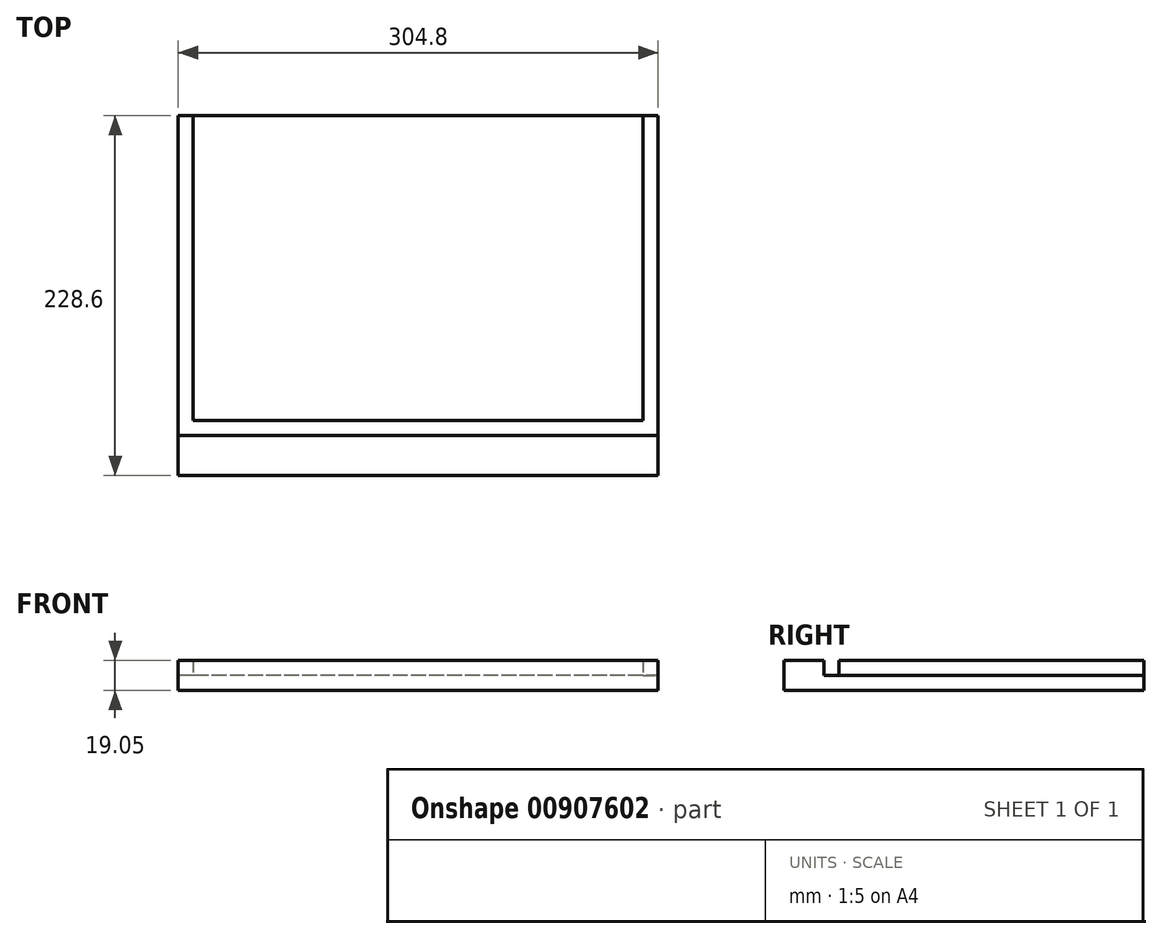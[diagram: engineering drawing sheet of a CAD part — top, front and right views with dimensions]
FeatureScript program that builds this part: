
annotation { "Feature Type Name" : "Feature", "Feature Type Description" : "" }
export const myFeature = defineFeature(function(context is Context, id is Id, definition is map)
    precondition{}
    {
        {
            var Q0;
            Q0=qCreatedBy(makeId("Top.planeOp"),FACE);
            var sketch = newSketch(context, id + "F0", { "sketchPlane" : qUnion([Q0])});
            skLineSegment(sketch, "E0.bottom", {"start": v(152.4, -114.3) * mm, "end": v(-152.4, -114.3) * mm});
            skLineSegment(sketch, "E0.top", {"start": v(152.4, 114.3) * mm, "end": v(-152.4, 114.3) * mm});
            skLineSegment(sketch, "E0.left", {"start": v(152.4, -114.3) * mm, "end": v(152.4, 114.3) * mm});
            skLineSegment(sketch, "E0.right", {"start": v(-152.4, -114.3) * mm, "end": v(-152.4, 114.3) * mm});
            skPoint(sketch, "E0.middle", {"position": v(0, 0) * mm});
            skSolve(sketch);
        }
        {
            var Q0;
            Q0 = qSketchRegion(id + "F0", true);
            extrude(context, id + "F1", {"entities" : qUnion([Q0]), "depth" : 19.05 * mm, "offsetDistance" : 25.4 * mm});
        }
        {
            var Q0;
            Q0=makeQuery(id+"F1.opExtrude","CAP_FACE",FACE,{"disambiguationData":[OSD([sQuery(id+"F0.wireOp",EDGE,"E0.bottom"),sQuery(id+"F0.wireOp",EDGE,"E0.top"),sQuery(id+"F0.wireOp",EDGE,"E0.left"),sQuery(id+"F0.wireOp",EDGE,"E0.right")])],"isStart":false});
            var sketch = newSketch(context, id + "F2", { "sketchPlane" : qUnion([Q0])});
            skLineSegment(sketch, "E1", {"start": v(0, -114.3) * mm, "end": v(0, -84.14) * mm});
            skLineSegment(sketch, "E2.bottom", {"start": v(188.14, -79.38) * mm, "end": v(-188.14, -79.38) * mm});
            skLineSegment(sketch, "E2.top", {"start": v(188.14, -88.9) * mm, "end": v(-188.14, -88.9) * mm});
            skLineSegment(sketch, "E2.left", {"start": v(188.14, -79.38) * mm, "end": v(188.14, -88.9) * mm});
            skLineSegment(sketch, "E2.right", {"start": v(-188.14, -79.38) * mm, "end": v(-188.14, -88.9) * mm});
            skPoint(sketch, "E2.middle", {"position": v(0, -84.14) * mm});
            skSolve(sketch);
        }
        {
            var Q0;
            Q0 = qSketchRegion(id + "F2", true);
            extrude(context, id + "F3", {"entities" : qUnion([Q0]), "operationType" : NewBodyOperationType.REMOVE, "oppositeDirection" : true, "depth" : 9.52 * mm, "offsetDistance" : 25.4 * mm});
        }
        {
            var Q0;
            Q0=makeQuery(id+"F1.opExtrude","SWEPT_FACE",FACE,{"disambiguationData":[OSD([sQuery(id+"F0.wireOp",EDGE,"E0.right")])]});
            var sketch = newSketch(context, id + "F4", { "sketchPlane" : qUnion([Q0])});
            skLineSegment(sketch, "E3.bottom", {"start": v(79.38, 28.57) * mm, "end": v(-114.3, 28.57) * mm});
            skLineSegment(sketch, "E3.top", {"start": v(79.38, 9.53) * mm, "end": v(-114.3, 9.53) * mm});
            skLineSegment(sketch, "E3.left", {"start": v(79.38, 28.57) * mm, "end": v(79.38, 9.53) * mm});
            skLineSegment(sketch, "E3.right", {"start": v(-114.3, 28.57) * mm, "end": v(-114.3, 9.53) * mm});
            skPoint(sketch, "E3.middle", {"position": v(-17.46, 19.05) * mm});
            skSolve(sketch);
        }
        {
            var Q0;
            Q0 = qSketchRegion(id + "F4", true);
            extrude(context, id + "F5", {"entities" : qUnion([Q0]), "operationType" : NewBodyOperationType.REMOVE, "oppositeDirection" : true, "depth" : 9.52 * mm, "offsetDistance" : 25.4 * mm});
        }
        {
            var Q0;
            Q0=makeQuery(id+"F1.opExtrude","SWEPT_FACE",FACE,{"disambiguationData":[OSD([sQuery(id+"F0.wireOp",EDGE,"E0.left")])]});
            var sketch = newSketch(context, id + "F6", { "sketchPlane" : qUnion([Q0])});
            skLineSegment(sketch, "E4.bottom", {"start": v(114.3, 28.57) * mm, "end": v(-79.38, 28.57) * mm});
            skLineSegment(sketch, "E4.top", {"start": v(114.3, 9.53) * mm, "end": v(-79.38, 9.53) * mm});
            skLineSegment(sketch, "E4.left", {"start": v(114.3, 28.57) * mm, "end": v(114.3, 9.53) * mm});
            skLineSegment(sketch, "E4.right", {"start": v(-79.38, 28.57) * mm, "end": v(-79.38, 9.53) * mm});
            skPoint(sketch, "E4.middle", {"position": v(17.46, 19.05) * mm});
            skSolve(sketch);
        }
        {
            var Q0;
            Q0 = qSketchRegion(id + "F6", true);
            extrude(context, id + "F7", {"entities" : qUnion([Q0]), "operationType" : NewBodyOperationType.REMOVE, "oppositeDirection" : true, "depth" : 9.52 * mm, "offsetDistance" : 25.4 * mm});
        }
    });
